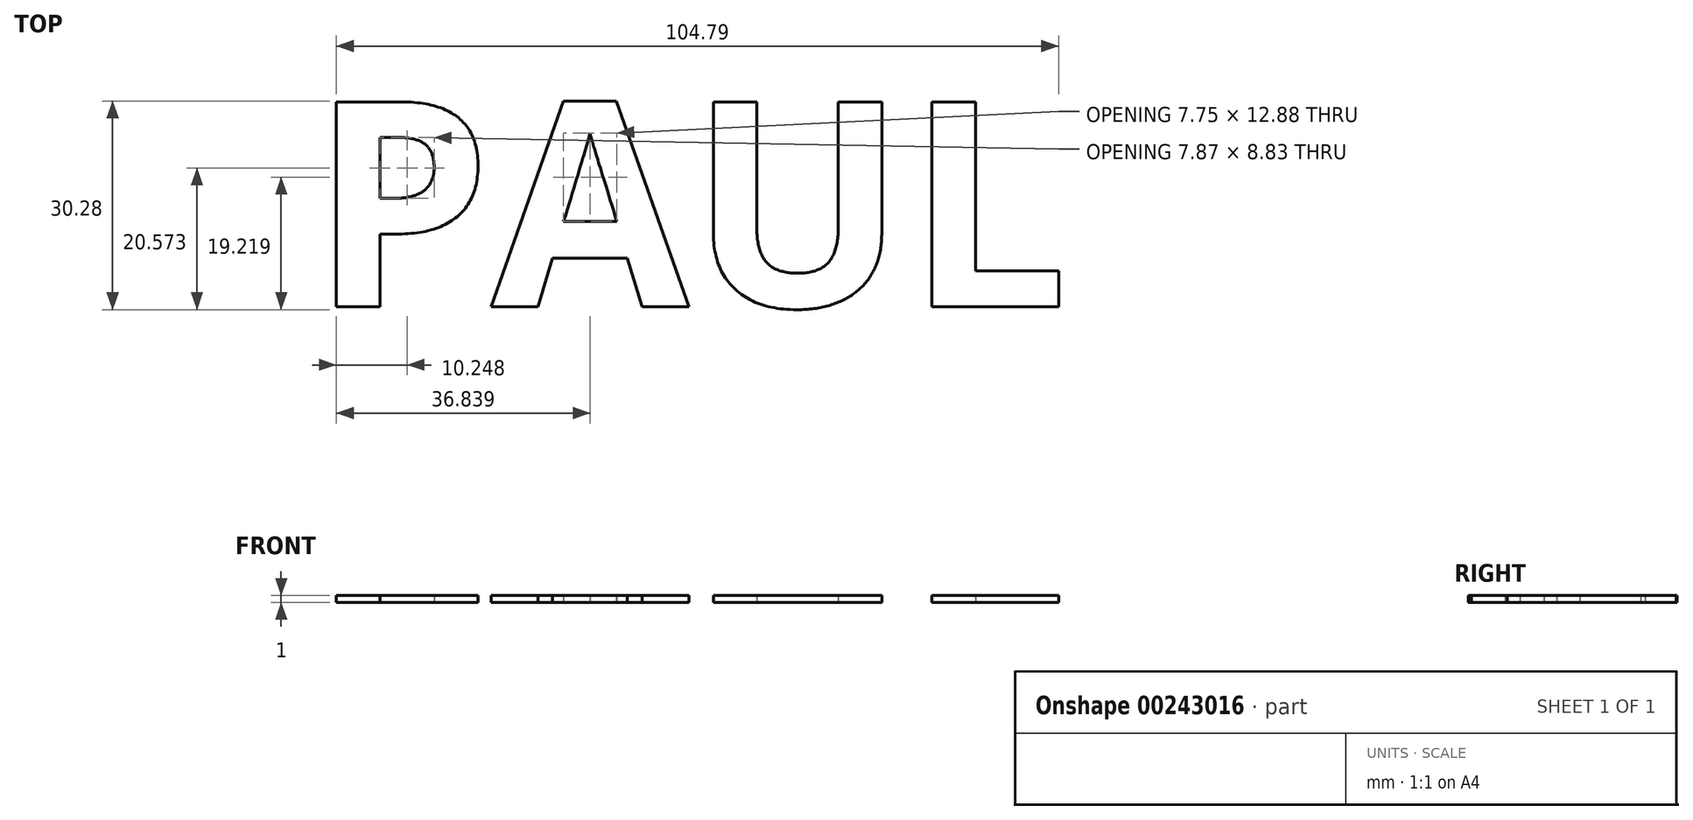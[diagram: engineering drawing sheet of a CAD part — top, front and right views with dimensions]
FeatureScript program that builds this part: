
annotation { "Feature Type Name" : "Feature", "Feature Type Description" : "" }
export const myFeature = defineFeature(function(context is Context, id is Id, definition is map)
    precondition{}
    {
        {
            var Q0;
            Q0=qCreatedBy(makeId("Top.planeOp"),FACE);
            var sketch = newSketch(context, id + "F0", { "sketchPlane" : qUnion([Q0])});
            skText(sketch, "E0", { "text": "PAUL", "fontName": "OpenSans-Bold.ttf"});
            const initialGuessF0  = {"E0": [-0.05562, 0, 1, 0, 0.03]};
            skSetInitialGuess(sketch, initialGuessF0);
            skSolve(sketch);
        }
        {
            var Q0;
            Q0 = qSketchRegion(id + "F0", true);
            extrude(context, id + "F1", {"entities" : qUnion([Q0]), "depth" : 1 * mm});
        }
    });
